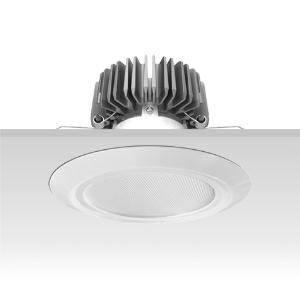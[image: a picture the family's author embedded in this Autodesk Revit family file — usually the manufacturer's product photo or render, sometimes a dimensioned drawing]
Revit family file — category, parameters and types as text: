
# Revit family: 3f_filippi_-_3f_reno_bianco_ampio_3f_filippi_-_30650_a01037_-_3f_reno_200_wh_2000-930_ep_wide___vs_wh_7420
name_source: partatom
category: Lighting Fixtures
units: mm (PartAtom-declared; Revit-internal decimal feet)

## family parameters
Cut with Voids When Loaded = No
Host = Face
Light Source = No
Part Type = Normal
Room Calculation Point = No
Round Connector Dimension = Use Diameter
Shared = No

## types (1)
- 3F Filippi - 3F Reno Bianco Ampio (1 x LED, 1650 lm, 25 W, 3000 K)
    Apparent Load = 25 VA
    Approval mark = ENEC
    CIE Flux Codes = 75 94 99 100 100
    Color Rendering = 90
    Color Temperature = 3000 K
    Control Gear = Electronic ballast
    Default Elevation = 1800 mm
    Description = ILLUMINOTECHNICAL
Luminous efficiency 100% (DLOR 100%, ULOR 0%).
Initial luminous flux of the luminaire 1650 lm.
Emergency luminaire luminous flux BLF 16.7%.
Direct symmetric wide distribution.
Installation Interdistance Transv.D = 1.16 x hu - Long.D = 1.14 x hu.
Average luminance <3000 cd/m² for radial angles >65°.
Tabular UGR (CIE 117 - 4H-8H; S=0.25H; 70/50/20): RUG 20.3 - 20.2.
Beam angle: 74° - 74°.
Luminous efficacy 66 lm/W.
Lifetime (L90/B10): 30000 h. (tq+25°C)
Lifetime (L85/B10): 50000 h. (tq+25°C)
Lifetime (L70/B10): 80000 h. (tq+25°C)
Sudden decreased luminous flux after 50000 hours: 0% (C0).
Photobiological safety in compliance with IEC/TR 62778: RG0 risk exempt, (IEC 62471).
In compliance with IEC/EN 62722-2-1 - IEC/EN 62717 standards.

SOURCE
Compact LED module 2000/930.
Energy efficiency class (UE 2019/2020 - UE 2019/2015): E.
CIE 13.3 Colour rendering index: CRI >90 (R9 >50%).
IES TM-30 Fidelity Index: Rf = 92 Rg = 101.
CCT nominal colour temperature 3000 K.
Colour initial tolerance (MacAdam): SDCM 3.
Zhaga Book 3 compliant.

MECHANICAL
Passive heat dissipator in die-casting aluminium, oversized, for optimum thermal management of the LED module.
Parabolic element with graduated/concentric rings in white polycarbonate.
Transparent external lens with glossy and satin differentiated surfaces, with a cooling and anti-insect system in methacrylate (PMMA).
Fastening spring clips in stainless steel.
Dimensions: diameter 226 mm, height 146 mm. Weight 1.71 kg.
IP44 protection degree for exposed part, IP20 for recessed part.
Mechanical strength to impacts IK06 (1 joule).
Glow-wire test resistance 650°C.

ELECTRICAL
Wiring on a separate unit.
Halogen Free electronic wiring 230V-50/60Hz, power factor 0.90, THD <25%, constant output current, SELV, class II, 1 driver.
Power of the luminaire 25 W.
CE - IEC 60598-1 - EN 60598-1.
EP maintained emergency wiring on board, 1h duration, 24h recharge; compliant with EN 60598-2-22, excluding high risk areas.
SAFE FLICKER: PstLM=<1 and SVM=<0.4 (IEC TR 61547-1 and IEC TR 63158), to ensure a more comfortable and safe light.
Ambient temperature from +5°C to +25°C.
Temperature class T6 max 85°C.
Relative humidity UR: <85%.

INSTALLATION
Pull-up recessed fitting.
False ceiling carving: 200 mm.
All accessories dedicated to this product are available on the Catalog and on our website www.3F-Filippi.com.

ACCESSORIES
A01037 - Anti-glare microprismatic VS moulded glass, tempered, not flammable, locked and in line with the trim, in white polycarbonate.

APPLICATIONS
Environments: architectural, commercial, exhibition areas, transit areas, corridors, shops, display windows, service areas.
In false ceilings with narrow voids.

WARNING
Luminaire designed for disposal/recycling at end-of-life.
Replaceable (LED only) light source by a professional. Replaceable control gear by a professional.
    Height = 0 mm  [stored 0 ft]
    Lamp = 1 x LED
    Lamp Light Flux = 1650 lm
    Lamp Power = 25 W
    Lamp count = 1
    Length = 226 mm
    Lifetime = 50000 h
    Luminous efficacy = 66 lm/W
    Manufacturer = 3F Filippi
    ModVariant = No
    Model = 3F Filippi - 30650+A01037 - 3F Reno 200 WH 2000-930 EP WIDE + VS WH
    Mounting Place = Ceiling
    Mounting Type = Recessed
    Number of Poles = 1
    OnlyDefault = Yes
    Power Factor = 1
    Product Name = 3F Filippi - 3F Reno Bianco Ampio
    Product group = recessed luminaire
    ProductGroupID = 4
    Protection Class = Protection class II
    Protection Degree = IP 20
    RLX_Detail_Level = 1
    RLX_Emergency_Light_Flux = 0 lm
    RLX_Emergency_Type = 0
    RLX_Emergency_Type_DB = No
    RlxData = <blob elided: 93641 chars, md5=ba33e744>
    Socket = socket
    Standby Power = 0 W
    System Light Flux = 1650 lm
    System Power = 25 W
    Type Comments = Product without accessories
    Type Image = 3ffilippi_3f_reno_200_wh_vs_smp.jpg
    URL = http://relux.com
    VarID = ---
    Voltage = 0 V
    Weight = 0.00 kg
    Width = 0 mm  [stored 0 ft]

note: [stored X ft] marks values corroborated as IEEE doubles in the binary element streams (Revit-internal decimal feet)

## geometry (parser evidence)
native form markers: Blend x4, Sweep x13
no freeform markers — native parametric forms only
